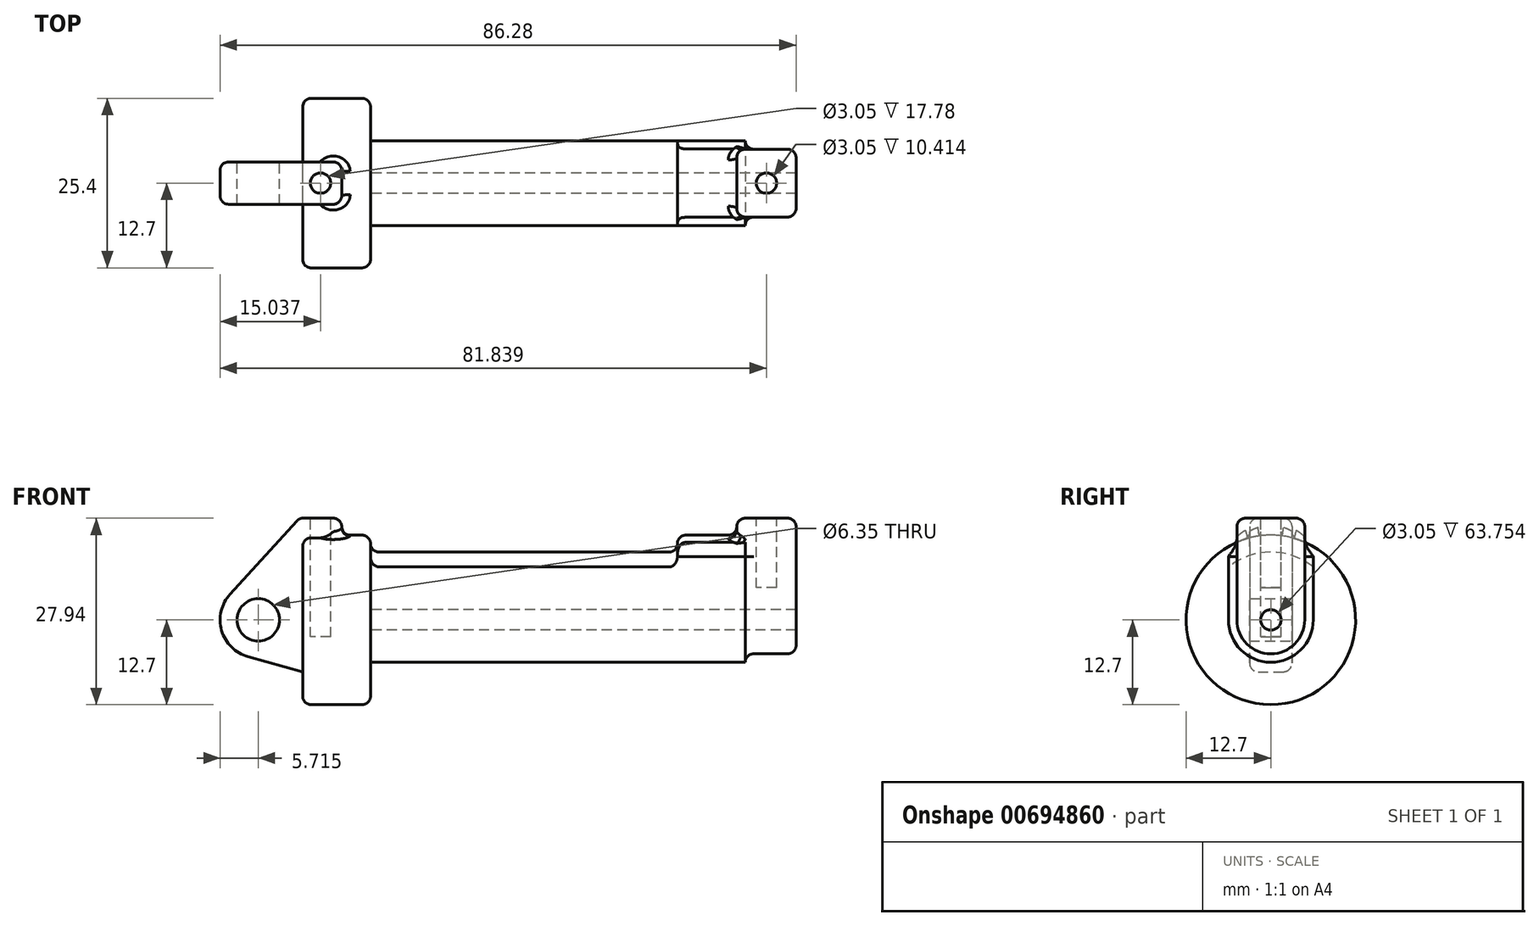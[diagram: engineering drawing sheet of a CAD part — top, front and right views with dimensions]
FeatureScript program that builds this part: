
annotation { "Feature Type Name" : "Feature", "Feature Type Description" : "" }
export const myFeature = defineFeature(function(context is Context, id is Id, definition is map)
    precondition{}
    {
        {
            var Q0;
            Q0=qCreatedBy(makeId("Front.planeOp"),FACE);
            var sketch = newSketch(context, id + "F0", { "sketchPlane" : qUnion([Q0])});
            skLineSegment(sketch, "E0", {"start": v(0, 0) * mm, "end": v(0, 12.7) * mm});
            skLineSegment(sketch, "E1", {"start": v(0, 12.7) * mm, "end": v(10.16, 12.7) * mm});
            skLineSegment(sketch, "E2", {"start": v(10.16, 12.7) * mm, "end": v(10.16, 10.16) * mm});
            skLineSegment(sketch, "E3", {"start": v(10.16, 10.16) * mm, "end": v(56.13, 10.16) * mm});
            skLineSegment(sketch, "E4", {"start": v(56.13, 10.16) * mm, "end": v(56.13, 12.7) * mm});
            skLineSegment(sketch, "E5", {"start": v(56.13, 12.7) * mm, "end": v(66.3, 12.7) * mm});
            skLineSegment(sketch, "E6", {"start": v(66.3, 12.7) * mm, "end": v(66.3, 0) * mm});
            skLineSegment(sketch, "E7", {"start": v(66.3, 0) * mm, "end": v(0, 0) * mm});
            skLineSegment(sketch, "E8", {"start": v(5.84, 15.24) * mm, "end": v(-0.5, 15.24) * mm});
            skLineSegment(sketch, "E9", {"start": v(-0.5, 15.24) * mm, "end": v(-10.88, 3.85) * mm});
            skLineSegment(sketch, "E10", {"start": v(0, 0) * mm, "end": v(-6.65, 0) * mm});
            skCircle(sketch, "E11", {"center": v(-6.65, 0) * mm, "radius": 5.72 * mm});
            skCircle(sketch, "E12", {"center": v(-6.65, 0) * mm, "radius": 3.18 * mm});
            skLineSegment(sketch, "E13", {"start": v(5.84, 15.24) * mm, "end": v(5.84, -9.4) * mm});
            skLineSegment(sketch, "E14", {"start": v(5.84, -9.4) * mm, "end": v(-8.18, -5.5) * mm});
            skSolve(sketch);
        }
        {
            var Q0;
            {var subQ0=sQuery(id+"F0.wireOp",EDGE,"E0");Q0=makeQuery(id+"F0.imprint","IMPRINT",FACE,{"disambiguationData":[TD([[makeQuery(id+"F0.imprint","IMPRINT",EDGE,{"derivedFrom":subQ0}),-1.0]])]});}
            var Q1;
            {var subQ0=sQuery(id+"F0.wireOp",EDGE,"E2");Q1=makeQuery(id+"F0.imprint","IMPRINT",FACE,{"disambiguationData":[TD([[makeQuery(id+"F0.imprint","IMPRINT",EDGE,{"derivedFrom":subQ0}),-1.0]])]});}
            var Q2;
            Q2=sQuery(id+"F0.wireOp",EDGE,"E7");
            revolve(context, id + "F1", {"entities" : qUnion([Q0, Q1]), "axis" : qUnion([Q2]), "revolveType" : RevolveType.FULL});
        }
        {
            var Q0;
            {var subQ5=sQuery(id+"F0.wireOp",EDGE,"E12");Q0=makeQuery(id+"F0.imprint","IMPRINT",FACE,{"disambiguationData":[TD([[makeQuery(id+"F0.imprint","IMPRINT",EDGE,{"derivedFrom":subQ5}),-1.0]])]});}
            var Q1;
            {var subQ1=sQuery(id+"F0.wireOp",EDGE,"E0");Q1=makeQuery(id+"F0.imprint","IMPRINT",FACE,{"disambiguationData":[TD([[makeQuery(id+"F0.imprint","IMPRINT",EDGE,{"derivedFrom":subQ1}),1.0]])]});}
            var Q2;
            {var subQ0=sQuery(id+"F0.wireOp",EDGE,"E14");Q2=makeQuery(id+"F0.imprint","IMPRINT",FACE,{"disambiguationData":[TD([[makeQuery(id+"F0.imprint","IMPRINT",EDGE,{"derivedFrom":subQ0}),-1.0]])]});}
            var Q3;
            {var subQ0=sQuery(id+"F0.wireOp",EDGE,"E0");Q3=makeQuery(id+"F0.imprint","IMPRINT",FACE,{"disambiguationData":[TD([[makeQuery(id+"F0.imprint","IMPRINT",EDGE,{"derivedFrom":subQ0}),-1.0]])]});}
            var Q4;
            Q4=sQuery(id+"F0.wireOp",EDGE,"E11");
            var Q5;
            Q5=sQuery(id+"F0.wireOp",EDGE,"E12");
            var Q6;
            Q6=sQuery(id+"F0.wireOp",EDGE,"E9");
            var Q7;
            Q7=sQuery(id+"F0.wireOp",EDGE,"E8");
            var Q8;
            Q8=sQuery(id+"F0.wireOp",EDGE,"E14");
            var Q9;
            Q9=sQuery(id+"F0.wireOp",EDGE,"E13");
            extrude(context, id + "F2", {"entities" : qUnion([Q0, Q1, Q2, Q3]), "operationType" : NewBodyOperationType.ADD, "surfaceEntities" : qUnion([Q4, Q5, Q6, Q7, Q8, Q9]), "depth" : 6.35 * mm, "offsetDistance" : 25.4 * mm, "symmetric" : true});
        }
        {
            var Q0;
            Q0=makeQuery(id+"F1.opRevolve","SWEPT_FACE",FACE,{"disambiguationData":[OSD([sQuery(id+"F0.wireOp",EDGE,"E6")])]});
            var sketch = newSketch(context, id + "F3", { "sketchPlane" : qUnion([Q0])});
            skCircle(sketch, "E15", {"center": v(0, 0) * mm, "radius": 5.08 * mm});
            skCircle(sketch, "E16", {"center": v(0, 0) * mm, "radius": 1.52 * mm});
            skLineSegment(sketch, "E17", {"start": v(-5.08, 0) * mm, "end": v(-5.08, 15.24) * mm});
            skLineSegment(sketch, "E18", {"start": v(-5.08, 15.24) * mm, "end": v(5.08, 15.24) * mm});
            skLineSegment(sketch, "E19", {"start": v(5.08, 15.24) * mm, "end": v(5.08, 0) * mm});
            skSolve(sketch);
        }
        {
            var Q0;
            {var subQ0=sQuery(id+"F3.wireOp",EDGE,"E18");Q0=makeQuery(id+"F3.imprint","IMPRINT",FACE,{"disambiguationData":[TD([[makeQuery(id+"F3.imprint","IMPRINT",EDGE,{"derivedFrom":subQ0}),-1.0]])]});}
            var Q1;
            {var subQ0=sQuery(id+"F3.wireOp",EDGE,"E17");var subQ1=sQuery(id+"F3.wireOp",EDGE,"E15");var subQ2=makeQuery(id+"F3.imprint","INTERSECT",VERTEX,{"derivedFrom":[subQ1,subQ0]});Q1=makeQuery(id+"F3.imprint","IMPRINT",FACE,{"disambiguationData":[TD([[makeQuery(id+"F3.imprint","IMPRINT",EDGE,{"disambiguationData":[TD([[subQ2,1.0]])],"derivedFrom":subQ1}),-1.0]])]});}
            var Q2;
            Q2=makeQuery(id+"F3.imprint","IMPRINT",FACE,{"disambiguationData":[TD([[makeQuery(id+"F3.imprint","IMPRINT",EDGE,{"derivedFrom":sQuery(id+"F3.wireOp",EDGE,"E16")}),-1.0]])]});
            extrude(context, id + "F4", {"entities" : qUnion([Q0, Q1, Q2]), "operationType" : NewBodyOperationType.ADD, "depth" : 7.62 * mm, "offsetDistance" : 25.4 * mm, "hasSecondDirection" : true, "secondDirectionOppositeDirection" : true, "secondDirectionDepth" : 1.27 * mm});
        }
        {
            var Q0;
            Q0=makeQuery(id+"F4.boolean.opBoolean","SPLIT",FACE,{"disambiguationData":[TD([makeQuery(id+"F4.opExtrude","SWEPT_FACE",FACE,{"disambiguationData":[OSD([sQuery(id+"F3.wireOp",EDGE,"E16")])]})])],"derivedFrom":makeQuery(id+"F1.opRevolve","SWEPT_FACE",FACE,{"disambiguationData":[OSD([sQuery(id+"F0.wireOp",EDGE,"E6")])]})});
            var Q1;
            Q1=makeQuery(id+"F1.opRevolve","SWEPT_FACE",FACE,{"disambiguationData":[OSD([sQuery(id+"F0.wireOp",EDGE,"E2")])]});
            extrude(context, id + "F5", {"entities" : qUnion([Q0]), "operationType" : NewBodyOperationType.REMOVE, "endBound" : BoundingType.UP_TO_SURFACE, "oppositeDirection" : true, "depth" : 25.4 * mm, "endBoundEntityFace" : qUnion([Q1]), "offsetDistance" : 25.4 * mm});
        }
        {
            var Q0;
            Q0=makeQuery(id+"F4.opExtrude","SWEPT_FACE",FACE,{"disambiguationData":[OSD([sQuery(id+"F3.wireOp",EDGE,"E18")])]});
            var sketch = newSketch(context, id + "F6", { "sketchPlane" : qUnion([Q0])});
            skCircle(sketch, "E20", {"center": v(69.47, 0) * mm, "radius": 1.52 * mm});
            skPoint(sketch, "E21", {"position": v(69.47, 5.08) * mm});
            skPoint(sketch, "E22", {"position": v(69.47, -5.08) * mm});
            skPoint(sketch, "E23", {"position": v(73.91, 0) * mm});
            skPoint(sketch, "E24", {"position": v(65.02, 0) * mm});
            skSolve(sketch);
        }
        {
            var Q0;
            Q0=makeQuery(id+"F2.opExtrude","SWEPT_FACE",FACE,{"disambiguationData":[OSD([sQuery(id+"F0.wireOp",EDGE,"E8")])]});
            var sketch = newSketch(context, id + "F7", { "sketchPlane" : qUnion([Q0])});
            skCircle(sketch, "E25", {"center": v(2.67, 0) * mm, "radius": 1.52 * mm});
            skPoint(sketch, "E26", {"position": v(2.67, 3.18) * mm});
            skPoint(sketch, "E27", {"position": v(5.84, 0) * mm});
            skSolve(sketch);
        }
        {
            var Q0;
            Q0=makeQuery(id+"F7.imprint","IMPRINT",FACE,{"disambiguationData":[TD([[makeQuery(id+"F7.imprint","IMPRINT",EDGE,{"derivedFrom":sQuery(id+"F7.wireOp",EDGE,"E25")}),1.0]])]});
            var Q1;
            Q1=sQuery(id+"F7.wireOp",EDGE,"E25");
            extrude(context, id + "F8", {"entities" : qUnion([Q0]), "operationType" : NewBodyOperationType.REMOVE, "surfaceEntities" : qUnion([Q1]), "oppositeDirection" : true, "depth" : 17.78 * mm, "offsetDistance" : 25.4 * mm});
        }
        {
            var Q0;
            Q0=makeQuery(id+"F6.imprint","IMPRINT",FACE,{"disambiguationData":[TD([[makeQuery(id+"F6.imprint","IMPRINT",EDGE,{"derivedFrom":sQuery(id+"F6.wireOp",EDGE,"E20")}),1.0]])]});
            extrude(context, id + "F9", {"entities" : qUnion([Q0]), "operationType" : NewBodyOperationType.REMOVE, "oppositeDirection" : true, "depth" : 10.4 * mm, "offsetDistance" : 25.4 * mm});
        }
        {
            var Q0;
            Q0=makeQuery(id+"F1.opRevolve","SWEPT_EDGE",EDGE,{"disambiguationData":[OSD([sQuery(id+"F0.wireOp",EDGE,"E5"),sQuery(id+"F0.wireOp",EDGE,"E6")])]});
            var Q1;
            Q1=makeQuery(id+"F1.opRevolve","SWEPT_EDGE",EDGE,{"disambiguationData":[OSD([sQuery(id+"F0.wireOp",EDGE,"E4"),sQuery(id+"F0.wireOp",EDGE,"E5")])]});
            var Q2;
            Q2=makeQuery(id+"F1.opRevolve","SWEPT_EDGE",EDGE,{"disambiguationData":[OSD([sQuery(id+"F0.wireOp",EDGE,"E1"),sQuery(id+"F0.wireOp",EDGE,"E2")])]});
            var Q3;
            Q3=makeQuery(id+"F1.opRevolve","SWEPT_EDGE",EDGE,{"disambiguationData":[OSD([sQuery(id+"F0.wireOp",EDGE,"E0"),sQuery(id+"F0.wireOp",EDGE,"E1")])]});
            var Q4;
            Q4=makeQuery(id+"F1.opRevolve","SWEPT_EDGE",EDGE,{"disambiguationData":[OSD([sQuery(id+"F0.wireOp",EDGE,"E2"),sQuery(id+"F0.wireOp",EDGE,"E3")])]});
            var Q5;
            Q5=makeQuery(id+"F1.opRevolve","SWEPT_EDGE",EDGE,{"disambiguationData":[OSD([sQuery(id+"F0.wireOp",EDGE,"E3"),sQuery(id+"F0.wireOp",EDGE,"E4")])]});
            fillet(context, id + "F10", {"entities" : qUnion([Q0, Q1, Q2, Q3, Q4, Q5]), "radius" : 1.27 * mm, "tangentPropagation" : true, "allowEdgeOverflow" : false});
        }
        {
            var Q0;
            Q0=makeQuery(id+"F4.opExtrude","SWEPT_EDGE",EDGE,{"disambiguationData":[OSD([sQuery(id+"F3.wireOp",EDGE,"E17"),sQuery(id+"F3.wireOp",EDGE,"E18")])]});
            var Q1;
            Q1=makeQuery(id+"F4.opExtrude","CAP_EDGE",EDGE,{"disambiguationData":[OSD([sQuery(id+"F3.wireOp",EDGE,"E18")])],"isStart":true});
            var Q2;
            Q2=makeQuery(id+"F4.boolean.opBoolean","INTERSECT",EDGE,{"derivedFrom":[makeQuery(id+"F1.opRevolve","SWEPT_FACE",FACE,{"disambiguationData":[OSD([sQuery(id+"F0.wireOp",EDGE,"E5")])]}),makeQuery(id+"F4.opExtrude","CAP_FACE",FACE,{"disambiguationData":[OSD([sQuery(id+"F3.wireOp",EDGE,"E15"),sQuery(id+"F3.wireOp",EDGE,"E16"),sQuery(id+"F3.wireOp",EDGE,"E17"),sQuery(id+"F3.wireOp",EDGE,"E18"),sQuery(id+"F3.wireOp",EDGE,"E19")])],"isStart":true})]});
            var Q3;
            Q3=makeQuery(id+"F4.opExtrude","CAP_EDGE",EDGE,{"disambiguationData":[OSD([sQuery(id+"F3.wireOp",EDGE,"E17")])],"isStart":false});
            var Q4;
            Q4=makeQuery(id+"F4.boolean.opBoolean","INTERSECT",EDGE,{"derivedFrom":[makeQuery(id+"F1.opRevolve","SWEPT_FACE",FACE,{"disambiguationData":[OSD([sQuery(id+"F0.wireOp",EDGE,"E6")])]}),makeQuery(id+"F4.opExtrude","SWEPT_FACE",FACE,{"disambiguationData":[OSD([sQuery(id+"F3.wireOp",EDGE,"E15")])]})]});
            var Q5;
            Q5=makeQuery(id+"F4.opExtrude","SWEPT_EDGE",EDGE,{"disambiguationData":[OSD([sQuery(id+"F3.wireOp",EDGE,"E18"),sQuery(id+"F3.wireOp",EDGE,"E19")])]});
            var Q6;
            Q6=makeQuery(id+"F4.opExtrude","CAP_EDGE",EDGE,{"disambiguationData":[OSD([sQuery(id+"F3.wireOp",EDGE,"E18")])],"isStart":false});
            var Q7;
            Q7=makeQuery(id+"F4.opExtrude","CAP_EDGE",EDGE,{"disambiguationData":[OSD([sQuery(id+"F3.wireOp",EDGE,"E19")])],"isStart":true});
            var Q8;
            Q8=makeQuery(id+"F4.opExtrude","CAP_EDGE",EDGE,{"disambiguationData":[OSD([sQuery(id+"F3.wireOp",EDGE,"E17")])],"isStart":true});
            fillet(context, id + "F11", {"entities" : qUnion([Q0, Q1, Q2, Q3, Q4, Q5, Q6, Q7, Q8]), "radius" : 1.27 * mm, "tangentPropagation" : true, "allowEdgeOverflow" : false});
        }
        {
            var Q0;
            Q0=makeQuery(id+"F2.opExtrude","CAP_EDGE",EDGE,{"disambiguationData":[OSD([sQuery(id+"F0.wireOp",EDGE,"E13")])],"isStart":true});
            var Q1;
            Q1=makeQuery(id+"F2.opExtrude","CAP_EDGE",EDGE,{"disambiguationData":[OSD([sQuery(id+"F0.wireOp",EDGE,"E13")])],"isStart":false});
            var Q2;
            Q2=makeQuery(id+"F2.boolean.opBoolean","INTERSECT",EDGE,{"derivedFrom":[makeQuery(id+"F1.opRevolve","SWEPT_FACE",FACE,{"disambiguationData":[OSD([sQuery(id+"F0.wireOp",EDGE,"E1")])]}),makeQuery(id+"F2.opExtrude","SWEPT_FACE",FACE,{"disambiguationData":[OSD([sQuery(id+"F0.wireOp",EDGE,"E13")])]})]});
            var Q3;
            Q3=makeQuery(id+"F2.opExtrude","CAP_EDGE",EDGE,{"disambiguationData":[OSD([sQuery(id+"F0.wireOp",EDGE,"E9")])],"isStart":true});
            var Q4;
            Q4=makeQuery(id+"F2.opExtrude","CAP_EDGE",EDGE,{"disambiguationData":[OSD([sQuery(id+"F0.wireOp",EDGE,"E14")])],"isStart":false});
            var Q5;
            Q5=makeQuery(id+"F2.opExtrude","SWEPT_EDGE",EDGE,{"disambiguationData":[OSD([sQuery(id+"F0.wireOp",EDGE,"E8"),sQuery(id+"F0.wireOp",EDGE,"E9")])]});
            var Q6;
            Q6=makeQuery(id+"F2.opExtrude","CAP_EDGE",EDGE,{"disambiguationData":[OSD([sQuery(id+"F0.wireOp",EDGE,"E8")])],"isStart":true});
            var Q7;
            Q7=makeQuery(id+"F2.opExtrude","SWEPT_EDGE",EDGE,{"disambiguationData":[OSD([sQuery(id+"F0.wireOp",EDGE,"E8"),sQuery(id+"F0.wireOp",EDGE,"E13")])]});
            var Q8;
            Q8=makeQuery(id+"F2.opExtrude","CAP_EDGE",EDGE,{"disambiguationData":[OSD([sQuery(id+"F0.wireOp",EDGE,"E8")])],"isStart":false});
            fillet(context, id + "F12", {"entities" : qUnion([Q0, Q1, Q2, Q3, Q4, Q5, Q6, Q7, Q8]), "radius" : 1.27 * mm, "tangentPropagation" : true, "allowEdgeOverflow" : false});
        }
    });
